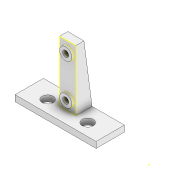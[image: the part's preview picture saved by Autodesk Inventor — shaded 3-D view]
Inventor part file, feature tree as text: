
AUTODESK INVENTOR PART (.ipt)
format: ipt  version: 2022 (Build 260153000, 153)  size: 219,136 bytes
history: native  units: mm
features: sketch x13, extrude x10, projected_geometry x7, split x1
ambient origin geometry x8: Origin, YZ Plane, XZ Plane, XY Plane, X Axis, Y Axis, Z Axis, Center Point
bodies: Solid1 (feature_tree), Solid2 (feature_tree), Solid3 (feature_tree)
feature tree (31):
  extrude  "Extrusion1"  Depth=50.0mm
  extrude  "Extrusion6"  Depth=5.5mm
  extrude  "Extrusion8"  Depth=3.0mm
  extrude  "Extrusion9"  Depth=4.0mm
  extrude  "Extrusion10"  Depth=30.0mm TaperAngle=0.0deg
  extrude  "Extrusion7"  Depth=1.0mm
  extrude  "Extrusion11"  Depth=10.0mm
  extrude  "Extrusion12"  Depth=3.0mm
  sketch  "Sketch13"  dims[d34=3.0mm d35=30.0mm d36=0.0mm]
  sketch  "Sketch14"  dims[d37=5.0mm d38=0.0mm d39=5.0mm d40=0.0mm]
  extrude  "Extrusion14"  Depth=30.0mm TaperAngle=0.0deg
  extrude  "Extrusion15"  Depth=5.0mm TaperAngle=0.0deg
  split  "Split1"
  sketch  "Sketch17"  dims[d44=6.0mm d45=6.0mm d46=1.0mm d47=0.0mm d48=2.0mm d49=0.0mm d52=10.0mm d53=0.0mm d54=2.0mm d55=0.0mm d56=0.0mm]
  sketch  "Sketch1"  dims[d0=25.0mm d1=50.0mm]
  sketch  "Sketch6"  dims[d2=5.5mm d3=5.5mm]
  sketch  "Sketch7"  dims[d4=3.0mm d5=0.0mm d22=3.0mm]
  sketch  "Sketch8"  dims[d23=4.0mm d24=4.0mm]
  projected_geometry  "Projected Loop3"
  sketch  "Sketch9"  dims[d25=6.0mm d26=30.0mm d27=0.0mm]
  projected_geometry  "Projected Loop4"
  sketch  "Sketch10"  dims[d28=1.0mm d29=1.0mm]
  sketch  "Sketch11"  dims[d30=10.0mm d31=20.0mm]
  sketch  "Sketch12"  dims[d32=4.0mm d33=3.0mm]
  projected_geometry  "Projected Loop5"
  projected_geometry  "Projected Loop6"
  sketch  "Sketch15"  dims[d41=4.0mm]
  sketch  "Sketch16"  dims[d42=8.0mm d43=0.0mm]
  projected_geometry  "Projected Loop7"
  projected_geometry  "Projected Loop8"
  projected_geometry  "Projected Loop9"
